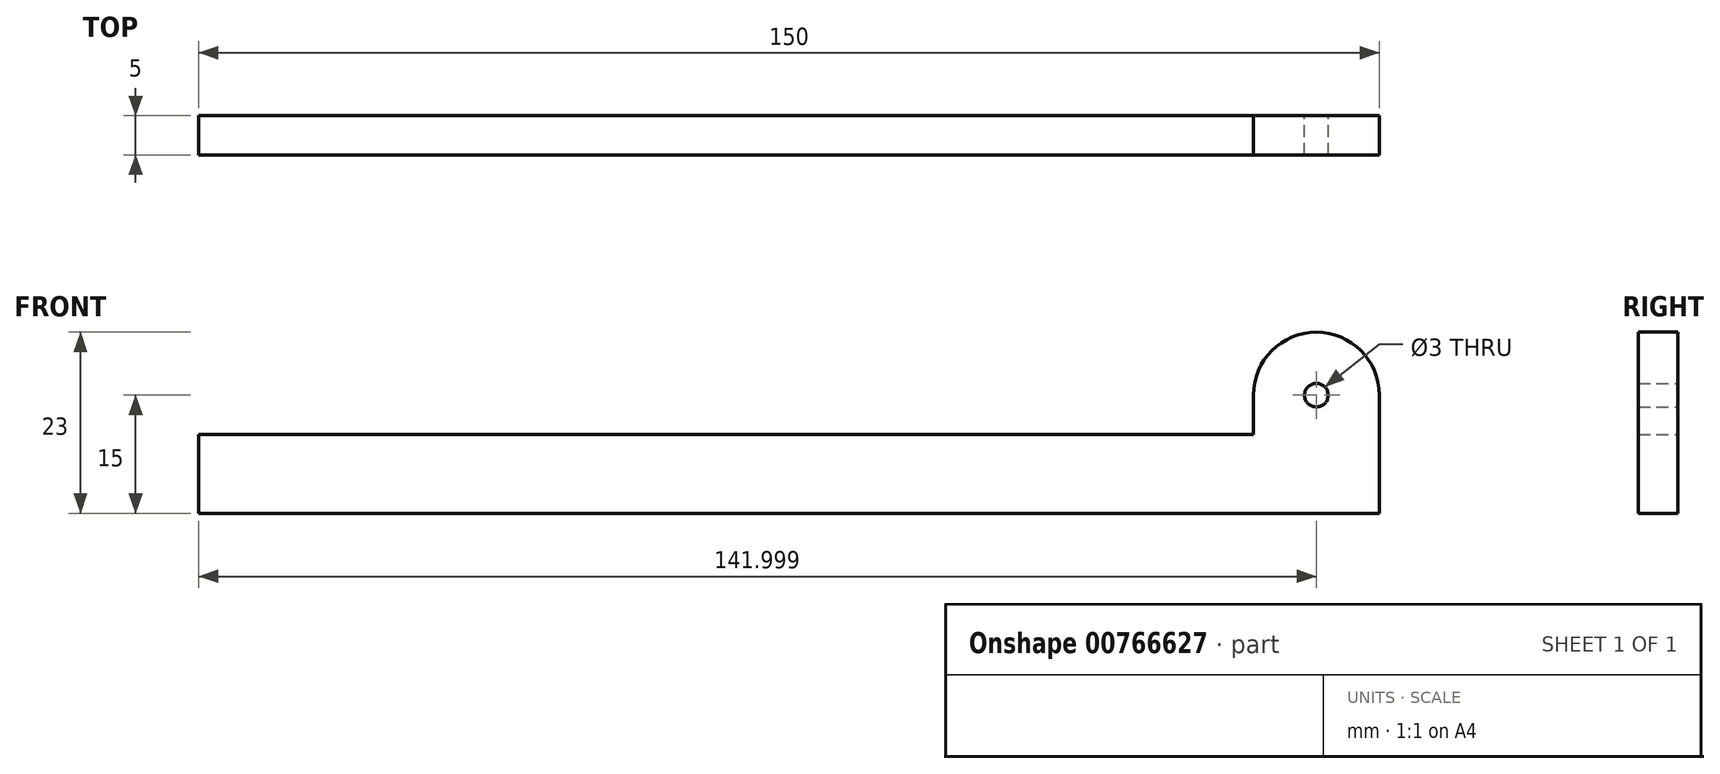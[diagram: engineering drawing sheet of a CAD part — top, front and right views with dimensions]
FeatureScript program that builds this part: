
annotation { "Feature Type Name" : "Feature", "Feature Type Description" : "" }
export const myFeature = defineFeature(function(context is Context, id is Id, definition is map)
    precondition{}
    {
        {
            var Q0;
            Q0=qCreatedBy(makeId("Front.planeOp"),FACE);
            var sketch = newSketch(context, id + "F0", { "sketchPlane" : qUnion([Q0])});
            skLineSegment(sketch, "E0.bottom", {"start": v(-72.91, 0) * mm, "end": v(77.09, 0) * mm});
            skLineSegment(sketch, "E0.top", {"start": v(-72.91, 10) * mm, "end": v(77.09, 10) * mm});
            skLineSegment(sketch, "E0.left", {"start": v(-72.91, 0) * mm, "end": v(-72.91, 10) * mm});
            skLineSegment(sketch, "E0.right", {"start": v(77.09, 0) * mm, "end": v(77.09, 10) * mm});
            skLineSegment(sketch, "E1", {"start": v(77.09, 10) * mm, "end": v(77.09, 15) * mm});
            skLineSegment(sketch, "E2", {"start": v(61.09, 10) * mm, "end": v(61.09, 15) * mm});
            skArc(sketch, "E3", {"start": v(77.09, 15) * mm, "mid": v(69.09, 23) * mm, "end": v(61.09, 15) * mm});
            skCircle(sketch, "E4", {"center": v(69.09, 15) * mm, "radius": 1.5 * mm});
            skSolve(sketch);
        }
        {
            var Q0;
            {var subQ0=sQuery(id+"F0.wireOp",EDGE,"E1");Q0=makeQuery(id+"F0.imprint","IMPRINT",FACE,{"disambiguationData":[TD([[makeQuery(id+"F0.imprint","IMPRINT",EDGE,{"derivedFrom":subQ0}),1.0]])]});}
            var Q1;
            Q1=makeQuery(id+"F0.imprint","IMPRINT",FACE,{"disambiguationData":[TD([[makeQuery(id+"F0.imprint","IMPRINT",EDGE,{"derivedFrom":sQuery(id+"F0.wireOp",EDGE,"E0.bottom")}),1.0]])]});
            extrude(context, id + "F1", {"entities" : qUnion([Q0, Q1]), "depth" : 5 * mm, "offsetDistance" : 25 * mm});
        }
    });
